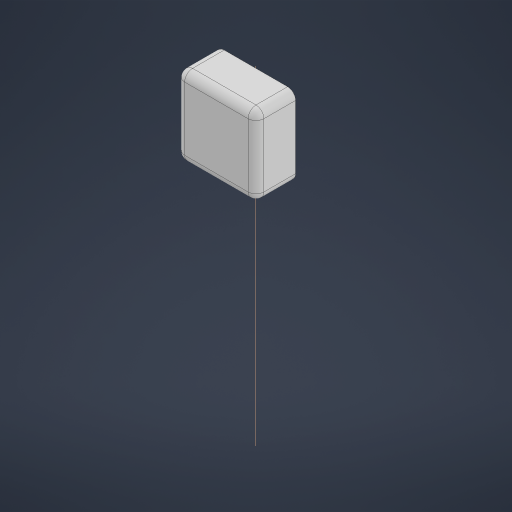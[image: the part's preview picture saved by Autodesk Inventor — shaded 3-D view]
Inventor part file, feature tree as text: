
AUTODESK INVENTOR PART (.ipt)
format: ipt  version: 2024.1 (Build 281209000, 209)  size: 2,138,112 bytes
history: native  units: mm
features: projected_geometry x5, fillet x4, other x3, extrude x3, sketch x3, boolean_combine x1, plane x1
ambient origin geometry x8: Origin, YZ Plane, XZ Plane, XY Plane, X Axis, Y Axis, Z Axis, Center Point
bodies: Solid2 (feature_tree), Solid1 (feature_tree)
feature tree (20):
  other  "TubeHolder YN Continuation.ipt"
  extrude  "Extrusion1"  Depth=30.0mm
  boolean_combine  "Combine1"
  plane  "Work Plane1"
  extrude  "Extrusion2"  Depth=10.0mm TaperAngle=0.0deg
  extrude  "Extrusion3"  TaperAngle=0.0deg  [1 undecoded]
  fillet  "Fillet1"  Radius=13.0mm
  fillet  "Fillet2"  Radius=5.0mm
  fillet  "Fillet3"  Radius=2.0mm
  fillet  "Fillet4"  Radius=1.5mm
  other  "Solid1::TubeHolder YN Continuation.ipt"
  other  "TaggingFeature1"
  sketch  "Sketch2"  dims[d0=10.0mm d1=30.0mm]
  projected_geometry  "Projected Loop1"
  projected_geometry  "Projected Loop2"
  projected_geometry  "Projected Loop3"
  projected_geometry  "Projected Loop4"
  sketch  "Sketch3"  dims[d2=30.0mm d3=10.0mm d4=20.0mm d5=0.0mm d6=0.0mm]
  sketch  "Sketch4"  dims[d7=-18.015mm d8=0.0mm d9=0.0mm d10=13.0mm d11=5.0mm d12=0.0mm d13=2.0mm d14=1.5mm d15=3.0mm d16=1.0mm]
  projected_geometry  "Project Cut Edges1"
note: 1 required parameter value undecoded (feature->parameter linkage not recoverable at this tier; creation-order binding heuristic only, values carry confidence <= 0.55)
